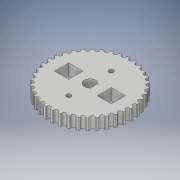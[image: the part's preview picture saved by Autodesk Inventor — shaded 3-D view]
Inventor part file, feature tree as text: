
AUTODESK INVENTOR PART (.ipt)
format: ipt  version: 2019 (Build 230136000, 136)  size: 336,384 bytes
history: native  units: mm
features: sketch x4, extrude x3, other x1, pattern_circular x1, hole x1
ambient origin geometry x8: Origin, YZ Plane, XZ Plane, XY Plane, X Axis, Y Axis, Z Axis, Center Point
bodies: Body1 (feature_tree)
feature tree (10):
  other  "ソリッド1"
  extrude  "押し出し1"  Depth=60.48mm
  pattern_circular  "円形状パターン1"  [2 undecoded]
  extrude  "押し出し2"  Depth=55.48mm
  extrude  "押し出し3"  Depth=2.74mm
  hole  "穴1"  [1 undecoded]
  sketch  "スケッチ1"
  sketch  "スケッチ2"
  sketch  "スケッチ3"
  sketch  "スケッチ4"
note: 3 required parameter values undecoded (feature->parameter linkage not recoverable at this tier; creation-order binding heuristic only, values carry confidence <= 0.55)
